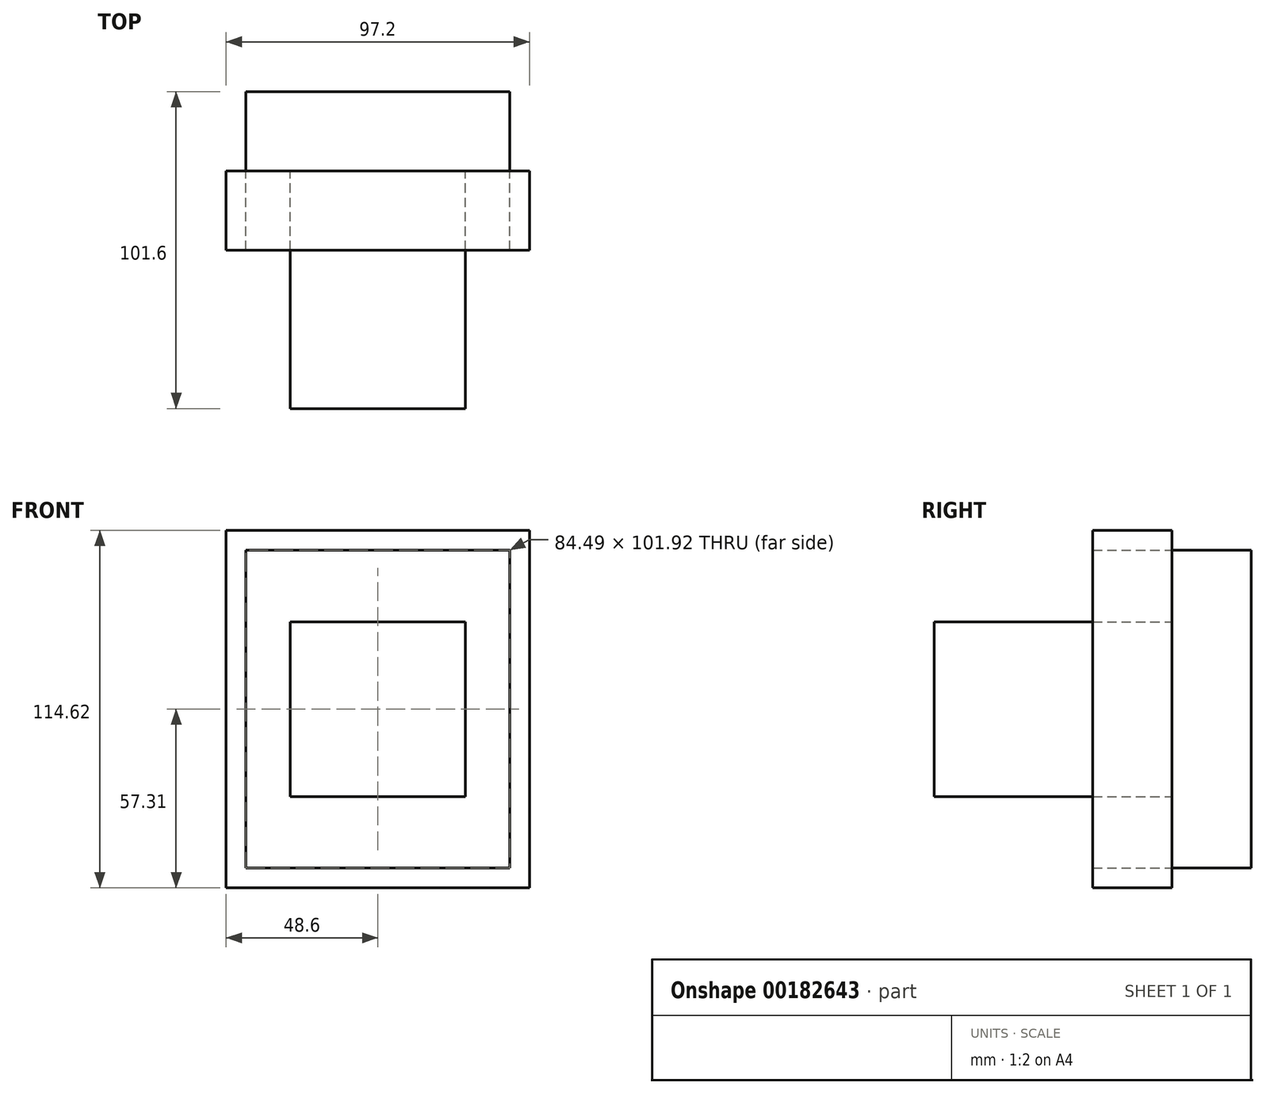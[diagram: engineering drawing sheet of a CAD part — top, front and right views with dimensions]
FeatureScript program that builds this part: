
annotation { "Feature Type Name" : "Feature", "Feature Type Description" : "" }
export const myFeature = defineFeature(function(context is Context, id is Id, definition is map)
    precondition{}
    {
        {
            var Q0;
            Q0=qCreatedBy(makeId("Front.planeOp"),FACE);
            var sketch = newSketch(context, id + "F0", { "sketchPlane" : qUnion([Q0])});
            skLineSegment(sketch, "E0.bottom", {"start": v(42.25, -50.96) * mm, "end": v(-42.25, -50.96) * mm});
            skLineSegment(sketch, "E0.top", {"start": v(42.25, 50.96) * mm, "end": v(-42.25, 50.96) * mm});
            skLineSegment(sketch, "E0.left", {"start": v(42.25, -50.96) * mm, "end": v(42.25, 50.96) * mm});
            skLineSegment(sketch, "E0.right", {"start": v(-42.25, -50.96) * mm, "end": v(-42.25, 50.96) * mm});
            skPoint(sketch, "E0.middle", {"position": v(0, 0) * mm});
            skSolve(sketch);
        }
        {
            var Q0;
            Q0 = qSketchRegion(id + "F0", true);
            extrude(context, id + "F1", {"entities" : qUnion([Q0]), "depth" : 25.4 * mm});
        }
        {
            var Q0;
            Q0=makeQuery(id+"F1.opExtrude","CAP_FACE",FACE,{"disambiguationData":[OSD([sQuery(id+"F0.wireOp",EDGE,"E0.bottom"),sQuery(id+"F0.wireOp",EDGE,"E0.top"),sQuery(id+"F0.wireOp",EDGE,"E0.left"),sQuery(id+"F0.wireOp",EDGE,"E0.right")])],"isStart":false});
            var sketch = newSketch(context, id + "F2", { "sketchPlane" : qUnion([Q0])});
            skLineSegment(sketch, "E1.0", {"start": v(48.6, 57.3) * mm, "end": v(-48.6, 57.3) * mm});
            skLineSegment(sketch, "E1.1", {"start": v(48.6, -57.3) * mm, "end": v(48.6, 57.3) * mm});
            skLineSegment(sketch, "E1.2", {"start": v(48.6, -57.3) * mm, "end": v(-48.6, -57.3) * mm});
            skLineSegment(sketch, "E1.3", {"start": v(-48.6, -57.3) * mm, "end": v(-48.6, 57.3) * mm});
            skSolve(sketch);
        }
        {
            var Q0;
            Q0=makeQuery(id+"F2.imprint","IMPRINT",FACE,{"disambiguationData":[TD([[makeQuery(id+"F2.imprint","IMPRINT",EDGE,{"derivedFrom":sQuery(id+"F2.wireOp",EDGE,"E1.0")}),1.0]])]});
            extrude(context, id + "F3", {"entities" : qUnion([Q0]), "depth" : 25.4 * mm});
        }
        {
            var Q0;
            Q0=makeQuery(id+"F1.opExtrude","CAP_FACE",FACE,{"disambiguationData":[OSD([sQuery(id+"F0.wireOp",EDGE,"E0.bottom"),sQuery(id+"F0.wireOp",EDGE,"E0.top"),sQuery(id+"F0.wireOp",EDGE,"E0.left"),sQuery(id+"F0.wireOp",EDGE,"E0.right")])],"isStart":false});
            var sketch = newSketch(context, id + "F4", { "sketchPlane" : qUnion([Q0])});
            skLineSegment(sketch, "E2.bottom", {"start": v(-28.01, -28.01) * mm, "end": v(28.01, -28.01) * mm});
            skLineSegment(sketch, "E2.top", {"start": v(-28.01, 28.01) * mm, "end": v(28.01, 28.01) * mm});
            skLineSegment(sketch, "E2.left", {"start": v(-28.01, -28.01) * mm, "end": v(-28.01, 28.01) * mm});
            skLineSegment(sketch, "E2.right", {"start": v(28.01, -28.01) * mm, "end": v(28.01, 28.01) * mm});
            skPoint(sketch, "E2.middle", {"position": v(0, 0) * mm});
            skSolve(sketch);
        }
        {
            var Q0;
            Q0=makeQuery(id+"F4.imprint","IMPRINT",FACE,{"disambiguationData":[TD([[makeQuery(id+"F4.imprint","IMPRINT",EDGE,{"derivedFrom":sQuery(id+"F4.wireOp",EDGE,"E2.bottom")}),1.0]])]});
            extrude(context, id + "F5", {"entities" : qUnion([Q0]), "operationType" : NewBodyOperationType.ADD, "depth" : 76.2 * mm});
        }
    });
